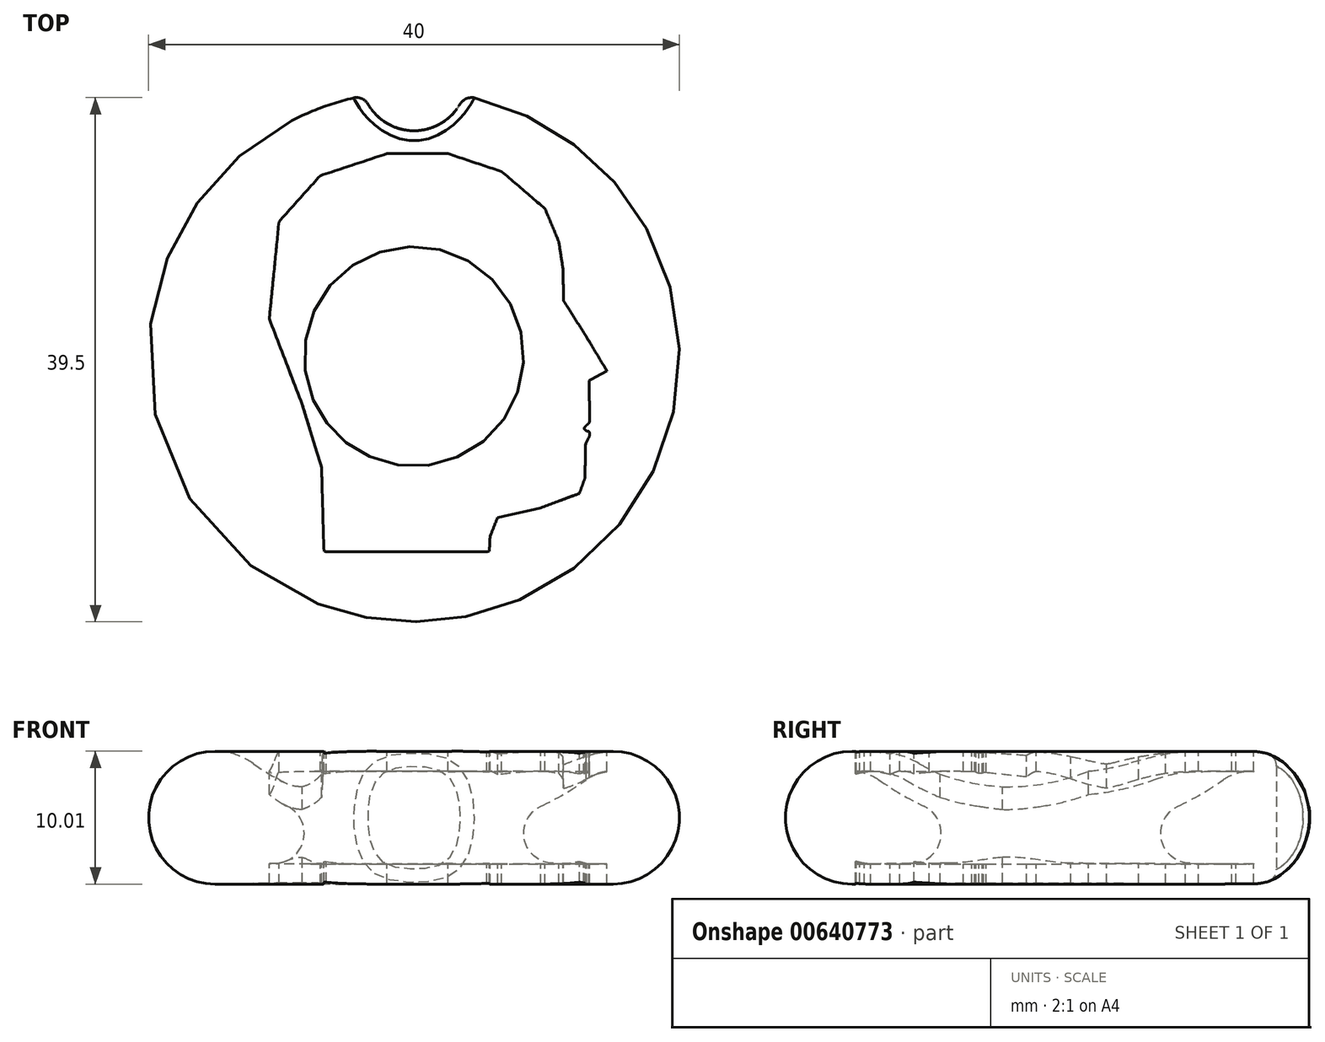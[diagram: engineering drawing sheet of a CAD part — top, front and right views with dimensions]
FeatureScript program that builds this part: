
annotation { "Feature Type Name" : "Feature", "Feature Type Description" : "" }
export const myFeature = defineFeature(function(context is Context, id is Id, definition is map)
    precondition{}
    {
        {
            var Q0;
            Q0=qCreatedBy(makeId("Front.planeOp"),FACE);
            var sketch = newSketch(context, id + "F0", { "sketchPlane" : qUnion([Q0])});
            skArc(sketch, "E0", {"start": v(-12.1, 8.86) * mm, "mid": v(-19.77, 6.27) * mm, "end": v(-14.93, -0.22) * mm});
            skArc(sketch, "E1", {"start": v(-12.1, 8.86) * mm, "mid": v(-6.35, 5.99) * mm, "end": v(0, 5) * mm});
            skLineSegment(sketch, "E2", {"start": v(-14.93, -0.22) * mm, "end": v(0, 0) * mm});
            skLineSegment(sketch, "E3", {"start": v(0, 0) * mm, "end": v(0, 5) * mm});
            skSolve(sketch);
        }
        {
            var Q0;
            Q0=makeQuery(id+"F0.imprint","IMPRINT",FACE,{"disambiguationData":[TD([[makeQuery(id+"F0.imprint","IMPRINT",EDGE,{"derivedFrom":sQuery(id+"F0.wireOp",EDGE,"E0")}),1.0]])]});
            var Q1;
            Q1=sQuery(id+"F0.wireOp",EDGE,"E3");
            revolve(context, id + "F1", {"entities" : qUnion([Q0]), "axis" : qUnion([Q1]), "revolveType" : RevolveType.FULL});
        }
        {
            var Q0;
            Q0=qCreatedBy(makeId("Top.planeOp"),FACE);
            cPlane(context, id + "F2", {"entities" : qUnion([Q0]), "cplaneType" : CPlaneType.OFFSET, "offset" : 10 * mm, "width" : 150 * mm, "height" : 150 * mm});
        }
        {
            var Q0;
            Q0=qCreatedBy(id+"F2.planeOp",FACE);
            var sketch = newSketch(context, id + "F3", { "sketchPlane" : qUnion([Q0])});
            skLineSegment(sketch, "E4", {"start": v(2.57, 15.27) * mm, "end": v(6.61, 13.92) * mm});
            skLineSegment(sketch, "E5", {"start": v(6.61, 13.92) * mm, "end": v(9.87, 11.13) * mm});
            skLineSegment(sketch, "E6", {"start": v(9.87, 11.13) * mm, "end": v(10.91, 8.64) * mm});
            skLineSegment(sketch, "E7", {"start": v(10.91, 8.64) * mm, "end": v(11.22, 6.62) * mm});
            skLineSegment(sketch, "E8", {"start": v(11.22, 6.62) * mm, "end": v(11.27, 4.18) * mm});
            skLineSegment(sketch, "E9", {"start": v(11.27, 4.18) * mm, "end": v(12.98, 1.49) * mm});
            skLineSegment(sketch, "E10", {"start": v(12.98, 1.49) * mm, "end": v(14.54, -1.1) * mm});
            skLineSegment(sketch, "E11", {"start": v(14.54, -1.1) * mm, "end": v(13.2, -1.83) * mm});
            skLineSegment(sketch, "E12", {"start": v(13.2, -1.83) * mm, "end": v(13.24, -4.88) * mm});
            skLineSegment(sketch, "E13", {"start": v(13.24, -4.88) * mm, "end": v(13.16, -5.07) * mm});
            skLineSegment(sketch, "E14", {"start": v(13.16, -5.07) * mm, "end": v(13, -5.17) * mm});
            skLineSegment(sketch, "E15", {"start": v(13, -5.17) * mm, "end": v(12.8, -5.43) * mm});
            skLineSegment(sketch, "E16", {"start": v(12.8, -5.43) * mm, "end": v(13, -5.64) * mm});
            skLineSegment(sketch, "E17", {"start": v(13, -5.64) * mm, "end": v(13.2, -5.66) * mm});
            skLineSegment(sketch, "E18", {"start": v(13.2, -5.66) * mm, "end": v(13.22, -5.74) * mm});
            skLineSegment(sketch, "E19", {"start": v(13.22, -5.74) * mm, "end": v(13.24, -5.97) * mm});
            skLineSegment(sketch, "E20", {"start": v(13.24, -5.97) * mm, "end": v(12.93, -6.6) * mm});
            skLineSegment(sketch, "E21", {"start": v(12.93, -6.6) * mm, "end": v(12.88, -9.19) * mm});
            skLineSegment(sketch, "E22", {"start": v(12.88, -9.19) * mm, "end": v(12.47, -10.33) * mm});
            skLineSegment(sketch, "E23", {"start": v(12.47, -10.33) * mm, "end": v(9.56, -11.41) * mm});
            skLineSegment(sketch, "E24", {"start": v(9.56, -11.41) * mm, "end": v(6.3, -12.14) * mm});
            skLineSegment(sketch, "E25", {"start": v(6.3, -12.14) * mm, "end": v(5.73, -13.59) * mm});
            skLineSegment(sketch, "E26", {"start": v(5.73, -13.59) * mm, "end": v(5.68, -14.68) * mm});
            skLineSegment(sketch, "E27", {"start": v(5.68, -14.68) * mm, "end": v(5.47, -14.73) * mm});
            skLineSegment(sketch, "E28", {"start": v(5.47, -14.73) * mm, "end": v(-6.6, -14.73) * mm});
            skLineSegment(sketch, "E29", {"start": v(-6.6, -14.73) * mm, "end": v(-6.76, -14.68) * mm});
            skLineSegment(sketch, "E30", {"start": v(-6.76, -14.68) * mm, "end": v(-6.8, -14.42) * mm});
            skLineSegment(sketch, "E31", {"start": v(-6.8, -14.42) * mm, "end": v(-6.8, -14.06) * mm});
            skLineSegment(sketch, "E32", {"start": v(-6.8, -14.06) * mm, "end": v(-6.96, -8.36) * mm});
            skLineSegment(sketch, "E33", {"start": v(-6.96, -8.36) * mm, "end": v(-8.42, -3.64) * mm});
            skLineSegment(sketch, "E34", {"start": v(-8.42, -3.64) * mm, "end": v(-10.9, 2.84) * mm});
            skLineSegment(sketch, "E35", {"start": v(-10.9, 2.84) * mm, "end": v(-10.18, 10.14) * mm});
            skLineSegment(sketch, "E36", {"start": v(-10.18, 10.14) * mm, "end": v(-7.07, 13.61) * mm});
            skLineSegment(sketch, "E37", {"start": v(-7.07, 13.61) * mm, "end": v(-2.04, 15.27) * mm});
            skLineSegment(sketch, "E38", {"start": v(-2.04, 15.27) * mm, "end": v(2.57, 15.27) * mm});
            skSolve(sketch);
        }
        {
            var Q0;
            Q0 = qSketchRegion(id + "F3", true);
            extrude(context, id + "F4", {"entities" : qUnion([Q0]), "operationType" : NewBodyOperationType.REMOVE, "oppositeDirection" : true, "depth" : 25 * mm, "offsetDistance" : 25 * mm});
        }
        {
            var Q0;
            Q0=qCreatedBy(makeId("Front.planeOp"),FACE);
            var sketch = newSketch(context, id + "F5", { "sketchPlane" : qUnion([Q0])});
            skLineSegment(sketch, "E39.0", {"start": v(-14.95, 1.28) * mm, "end": v(-10.5, 1.35) * mm});
            skArc(sketch, "E39.1", {"start": v(-12.97, 7.64) * mm, "mid": v(-18.34, 5.82) * mm, "end": v(-14.95, 1.28) * mm});
            skArc(sketch, "E39.2", {"start": v(-9.56, 5.64) * mm, "mid": v(-11.31, 6.56) * mm, "end": v(-12.97, 7.64) * mm});
            skLineSegment(sketch, "E40", {"start": v(-22.41, 25.6) * mm, "end": v(-22.06, 1.18) * mm});
            skArc(sketch, "E41", {"start": v(-10.5, 1.35) * mm, "mid": v(-8.32, 3.13) * mm, "end": v(-9.56, 5.64) * mm});
            skSolve(sketch);
        }
        {
            var Q0;
            Q0 = qSketchRegion(id + "F5", true);
            var Q1;
            Q1=sQuery(id+"F0.wireOp",EDGE,"E3");
            revolve(context, id + "F6", {"operationType" : NewBodyOperationType.ADD, "surfaceOperationType" : NewSurfaceOperationType.NEW, "entities" : qUnion([Q0]), "axis" : qUnion([Q1]), "revolveType" : RevolveType.FULL});
        }
        {
            var Q0;
            Q0=qCreatedBy(makeId("Top.planeOp"),FACE);
            cPlane(context, id + "F7", {"entities" : qUnion([Q0]), "cplaneType" : CPlaneType.OFFSET, "offset" : 25.14 * mm, "oppositeDirection" : true, "width" : 150 * mm, "height" : 150 * mm});
        }
        {
            var Q0;
            Q0=qCreatedBy(id+"F7.planeOp",FACE);
            var sketch = newSketch(context, id + "F8", { "sketchPlane" : qUnion([Q0])});
            skCircle(sketch, "E42", {"center": v(0, 21) * mm, "radius": 4 * mm});
            skSolve(sketch);
        }
        {
            var Q0;
            Q0 = qSketchRegion(id + "F8", true);
            extrude(context, id + "F9", {"entities" : qUnion([Q0]), "operationType" : NewBodyOperationType.REMOVE, "depth" : 126.55 * mm, "offsetDistance" : 25 * mm});
        }
        {
            var Q0;
            Q0=makeQuery(id+"F9.boolean.opBoolean","INTERSECT",EDGE,{"derivedFrom":[makeQuery(id+"F1.opRevolve","SWEPT_FACE",FACE,{"disambiguationData":[OSD([sQuery(id+"F0.wireOp",EDGE,"E0")])]}),makeQuery(id+"F9.opExtrude","SWEPT_FACE",FACE,{"disambiguationData":[OSD([sQuery(id+"F8.wireOp",EDGE,"E42")])]})]});
            fillet(context, id + "F10", {"entities" : qUnion([Q0]), "radius" : 1 * mm, "tangentPropagation" : true, "allowEdgeOverflow" : false});
        }
    });
